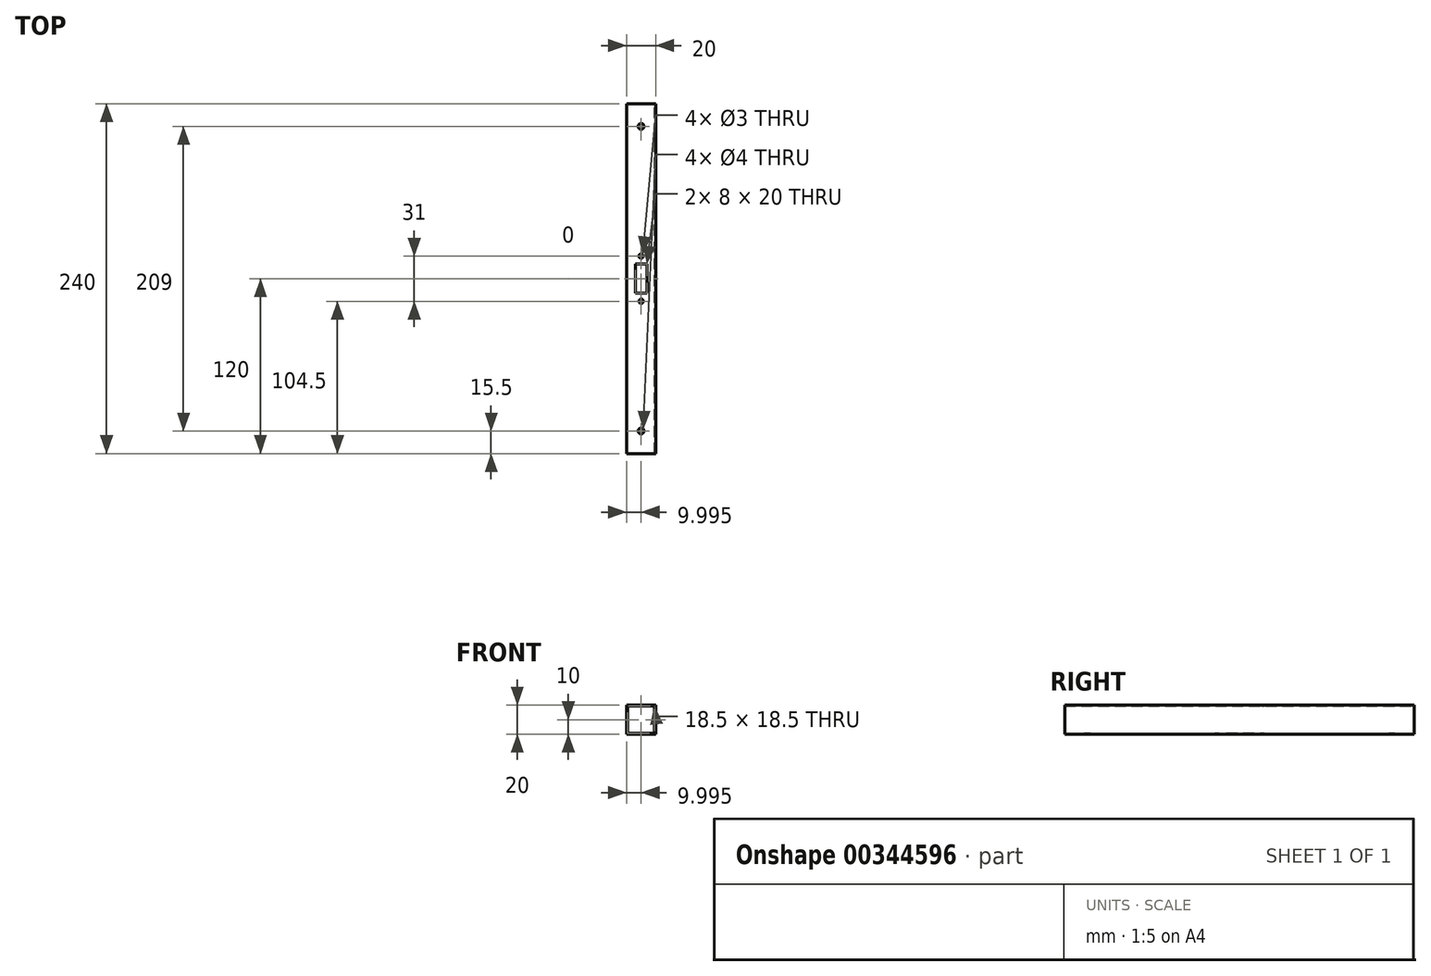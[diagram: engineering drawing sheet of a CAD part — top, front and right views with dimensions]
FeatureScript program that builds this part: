
annotation { "Feature Type Name" : "Feature", "Feature Type Description" : "" }
export const myFeature = defineFeature(function(context is Context, id is Id, definition is map)
    precondition{}
    {
        {
            var Q0;
            Q0=qCreatedBy(makeId("Front.planeOp"),FACE);
            var sketch = newSketch(context, id + "F0", { "sketchPlane" : qUnion([Q0])});
            skLineSegment(sketch, "E0.bottom", {"start": v(-34.48, 27) * mm, "end": v(-54.48, 27) * mm});
            skLineSegment(sketch, "E0.top", {"start": v(-34.48, 47) * mm, "end": v(-54.48, 47) * mm});
            skLineSegment(sketch, "E0.left", {"start": v(-34.48, 27) * mm, "end": v(-34.48, 47) * mm});
            skLineSegment(sketch, "E0.right", {"start": v(-54.48, 27) * mm, "end": v(-54.48, 47) * mm});
            skPoint(sketch, "E0.middle", {"position": v(-44.48, 37) * mm});
            skLineSegment(sketch, "E1.bottom", {"start": v(-35.23, 27.75) * mm, "end": v(-53.73, 27.75) * mm});
            skLineSegment(sketch, "E1.top", {"start": v(-35.23, 46.25) * mm, "end": v(-53.73, 46.25) * mm});
            skLineSegment(sketch, "E1.left", {"start": v(-35.23, 27.75) * mm, "end": v(-35.23, 46.25) * mm});
            skLineSegment(sketch, "E1.right", {"start": v(-53.73, 27.75) * mm, "end": v(-53.73, 46.25) * mm});
            skSolve(sketch);
        }
        {
            var Q0;
            Q0=makeQuery(id+"F0.imprint","IMPRINT",FACE,{"disambiguationData":[TD([[makeQuery(id+"F0.imprint","IMPRINT",EDGE,{"derivedFrom":sQuery(id+"F0.wireOp",EDGE,"E0.bottom")}),-1.0]])]});
            extrude(context, id + "F1", {"entities" : qUnion([Q0]), "depth" : 240 * mm});
        }
        {
            var Q0;
            Q0=makeQuery(id+"F1.opExtrude","SWEPT_FACE",FACE,{"disambiguationData":[OSD([sQuery(id+"F0.wireOp",EDGE,"E0.top")])]});
            var sketch = newSketch(context, id + "F2", { "sketchPlane" : qUnion([Q0])});
            skLineSegment(sketch, "E2.bottom", {"start": v(-54.48, 0) * mm, "end": v(-34.48, 0) * mm});
            skLineSegment(sketch, "E2.top", {"start": v(-54.48, -240) * mm, "end": v(-34.48, -240) * mm});
            skLineSegment(sketch, "E2.left", {"start": v(-54.48, 0) * mm, "end": v(-54.48, -240) * mm});
            skLineSegment(sketch, "E2.right", {"start": v(-34.48, 0) * mm, "end": v(-34.48, -240) * mm});
            skLineSegment(sketch, "E3", {"start": v(-34.48, -120) * mm, "end": v(-54.48, -120) * mm});
            skLineSegment(sketch, "E4.bottom", {"start": v(-41.48, -129) * mm, "end": v(-47.48, -129) * mm});
            skLineSegment(sketch, "E4.top", {"start": v(-41.48, -111) * mm, "end": v(-47.48, -111) * mm});
            skLineSegment(sketch, "E4.left", {"start": v(-41.48, -129) * mm, "end": v(-41.48, -111) * mm});
            skLineSegment(sketch, "E4.right", {"start": v(-47.48, -129) * mm, "end": v(-47.48, -111) * mm});
            skPoint(sketch, "E4.middle", {"position": v(-44.48, -120) * mm});
            skLineSegment(sketch, "E5.bottom", {"start": v(-40.48, -130) * mm, "end": v(-48.48, -130) * mm});
            skLineSegment(sketch, "E5.top", {"start": v(-40.48, -110) * mm, "end": v(-48.48, -110) * mm});
            skLineSegment(sketch, "E5.left", {"start": v(-40.48, -130) * mm, "end": v(-40.48, -110) * mm});
            skLineSegment(sketch, "E5.right", {"start": v(-48.48, -130) * mm, "end": v(-48.48, -110) * mm});
            skLineSegment(sketch, "E6", {"start": v(-44.48, -130) * mm, "end": v(-44.48, -135.5) * mm});
            skPoint(sketch, "E6.endSnap0", {"position": v(-44.48, -130) * mm});
            skLineSegment(sketch, "E7", {"start": v(-44.48, -110) * mm, "end": v(-44.48, -104.5) * mm});
            skPoint(sketch, "E7.endSnap0", {"position": v(-44.48, -110) * mm});
            skCircle(sketch, "E8", {"center": v(-44.48, -104.5) * mm, "radius": 1.5 * mm});
            skCircle(sketch, "E9", {"center": v(-44.48, -135.5) * mm, "radius": 1.5 * mm});
            skSolve(sketch);
        }
        {
            var Q0;
            {var subQ5=sQuery(id+"F2.wireOp",EDGE,"E4.bottom");Q0=makeQuery(id+"F2.imprint","IMPRINT",FACE,{"disambiguationData":[TD([[makeQuery(id+"F2.imprint","IMPRINT",EDGE,{"derivedFrom":subQ5}),-1.0]])]});}
            var Q1;
            {var subQ5=sQuery(id+"F2.wireOp",EDGE,"E4.top");Q1=makeQuery(id+"F2.imprint","IMPRINT",FACE,{"disambiguationData":[TD([[makeQuery(id+"F2.imprint","IMPRINT",EDGE,{"derivedFrom":subQ5}),1.0]])]});}
            var Q2;
            {var subQ6=sQuery(id+"F2.wireOp",EDGE,"E4.top");Q2=makeQuery(id+"F2.imprint","IMPRINT",FACE,{"disambiguationData":[TD([[makeQuery(id+"F2.imprint","IMPRINT",EDGE,{"derivedFrom":subQ6}),-1.0]])]});}
            var Q3;
            {var subQ0=sQuery(id+"F2.wireOp",EDGE,"E4.bottom");Q3=makeQuery(id+"F2.imprint","IMPRINT",FACE,{"disambiguationData":[TD([[makeQuery(id+"F2.imprint","IMPRINT",EDGE,{"derivedFrom":subQ0}),1.0]])]});}
            var Q4;
            Q4=makeQuery(id+"F2.imprint","IMPRINT",FACE,{"disambiguationData":[TD([[makeQuery(id+"F2.imprint","IMPRINT",EDGE,{"derivedFrom":sQuery(id+"F2.wireOp",EDGE,"E8")}),1.0]])]});
            var Q5;
            Q5=makeQuery(id+"F2.imprint","IMPRINT",FACE,{"disambiguationData":[TD([[makeQuery(id+"F2.imprint","IMPRINT",EDGE,{"derivedFrom":sQuery(id+"F2.wireOp",EDGE,"E9")}),1.0]])]});
            extrude(context, id + "F3", {"entities" : qUnion([Q0, Q1, Q2, Q3, Q4, Q5]), "operationType" : NewBodyOperationType.REMOVE, "oppositeDirection" : true, "depth" : 25 * mm});
        }
        {
            var Q0;
            Q0=makeQuery(id+"F1.opExtrude","SWEPT_FACE",FACE,{"disambiguationData":[OSD([sQuery(id+"F0.wireOp",EDGE,"E0.top")])]});
            var sketch = newSketch(context, id + "F4", { "sketchPlane" : qUnion([Q0])});
            skLineSegment(sketch, "E10", {"start": v(-44.48, 0) * mm, "end": v(-44.48, -15.5) * mm});
            skLineSegment(sketch, "E11", {"start": v(-44.48, -240) * mm, "end": v(-44.48, -224.5) * mm});
            skCircle(sketch, "E12", {"center": v(-44.48, -224.5) * mm, "radius": 2 * mm});
            skCircle(sketch, "E13", {"center": v(-44.48, -15.5) * mm, "radius": 2 * mm});
            skSolve(sketch);
        }
        {
            var Q0;
            Q0 = qSketchRegion(id + "F4", true);
            extrude(context, id + "F5", {"entities" : qUnion([Q0]), "operationType" : NewBodyOperationType.REMOVE, "oppositeDirection" : true, "depth" : 25 * mm});
        }
    });
